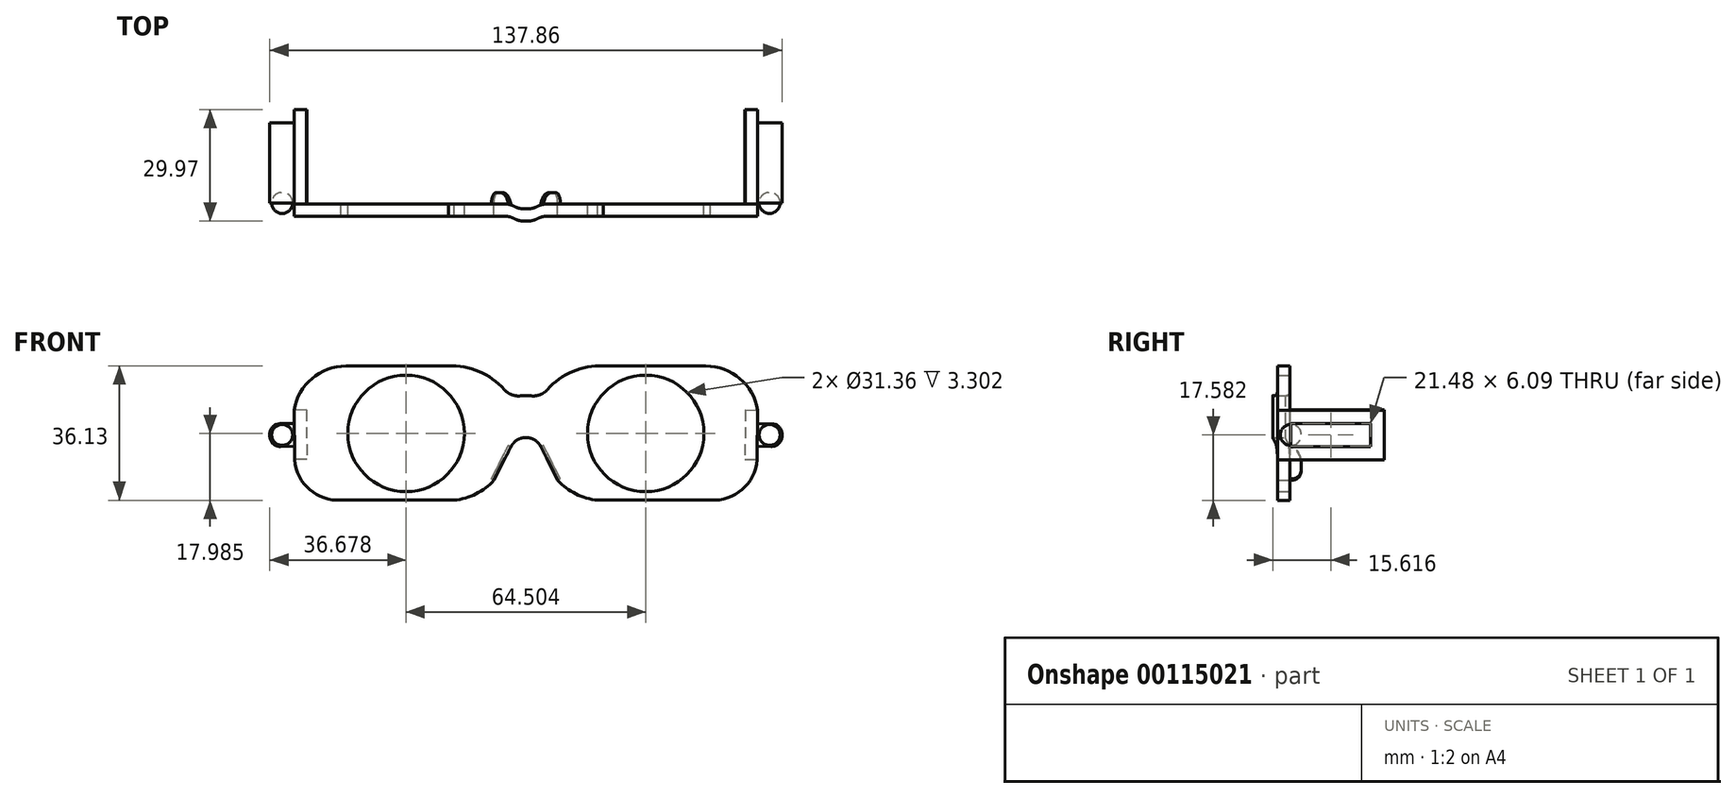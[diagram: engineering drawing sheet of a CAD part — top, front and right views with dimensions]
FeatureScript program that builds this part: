
annotation { "Feature Type Name" : "Feature", "Feature Type Description" : "" }
export const myFeature = defineFeature(function(context is Context, id is Id, definition is map)
    precondition{}
    {
        {
            var Q0;
            Q0=qCreatedBy(makeId("Front.planeOp"),FACE);
            var sketch = newSketch(context, id + "F0", { "sketchPlane" : qUnion([Q0])});
            skArc(sketch, "E0", {"start": v(-62.23, -1.34) * mm, "mid": v(-58.21, -9.35) * mm, "end": v(-49.73, -12.25) * mm});
            skArc(sketch, "E1", {"start": v(-19.33, -12.25) * mm, "mid": v(-13.44, -10.57) * mm, "end": v(-8.57, -6.88) * mm});
            skLineSegment(sketch, "E2", {"start": v(-4, 2.15) * mm, "end": v(-8.57, -6.88) * mm});
            skArc(sketch, "E3.MirrorCS", {"start": v(19.33, -12.25) * mm, "mid": v(13.44, -10.57) * mm, "end": v(8.57, -6.88) * mm});
            skLineSegment(sketch, "E4", {"start": v(4.02, 2.15) * mm, "end": v(8.57, -6.88) * mm});
            skLineSegment(sketch, "E5", {"start": v(-49.73, -12.25) * mm, "end": v(-19.33, -12.25) * mm});
            skArc(sketch, "E6.MirrorCS", {"start": v(62.23, -1.34) * mm, "mid": v(58.21, -9.35) * mm, "end": v(49.73, -12.25) * mm});
            skLineSegment(sketch, "E7", {"start": v(19.33, -12.25) * mm, "end": v(49.73, -12.25) * mm});
            skArc(sketch, "E8", {"start": v(-48.38, 23.83) * mm, "mid": v(-57.58, 20.47) * mm, "end": v(-62.41, 11.96) * mm});
            skLineSegment(sketch, "E9", {"start": v(-62.41, 11.96) * mm, "end": v(-62.23, -1.34) * mm});
            skArc(sketch, "E10.MirrorCS", {"start": v(48.38, 23.83) * mm, "mid": v(57.58, 20.47) * mm, "end": v(62.41, 11.96) * mm});
            skLineSegment(sketch, "E11", {"start": v(62.41, 11.96) * mm, "end": v(62.23, -1.34) * mm});
            skArc(sketch, "E12", {"start": v(4.02, 2.15) * mm, "mid": v(0.01, 4.62) * mm, "end": v(-4, 2.15) * mm});
            skArc(sketch, "E13", {"start": v(-4, 15.1) * mm, "mid": v(-11.25, 21.75) * mm, "end": v(-20.87, 23.83) * mm});
            skArc(sketch, "E14.MirrorCS", {"start": v(4, 15.1) * mm, "mid": v(11.25, 21.75) * mm, "end": v(20.87, 23.83) * mm});
            skLineSegment(sketch, "E15", {"start": v(-48.38, 23.83) * mm, "end": v(-20.87, 23.83) * mm});
            skLineSegment(sketch, "E16", {"start": v(20.87, 23.83) * mm, "end": v(48.38, 23.83) * mm});
            skArc(sketch, "E17", {"start": v(4, 15.1) * mm, "mid": v(0, 15.92) * mm, "end": v(-4, 15.1) * mm});
            skLineSegment(sketch, "E18", {"start": v(-32.25, 21.4) * mm, "end": v(-32.25, -9.96) * mm});
            skLineSegment(sketch, "E19", {"start": v(32.25, 21.4) * mm, "end": v(32.25, -9.96) * mm});
            skArc(sketch, "E20", {"start": v(-32.25, 21.4) * mm, "mid": v(-47.93, 5.71) * mm, "end": v(-32.25, -9.96) * mm});
            skArc(sketch, "E21.MirrorCS", {"start": v(-32.25, 21.4) * mm, "mid": v(-16.57, 5.71) * mm, "end": v(-32.25, -9.96) * mm});
            skArc(sketch, "E22.MirrorCS", {"start": v(32.25, 21.4) * mm, "mid": v(47.93, 5.71) * mm, "end": v(32.25, -9.96) * mm});
            skArc(sketch, "E23.MirrorCS", {"start": v(32.25, 21.4) * mm, "mid": v(16.57, 5.71) * mm, "end": v(32.25, -9.96) * mm});
            skSolve(sketch);
        }
        {
            var Q0;
            Q0=makeQuery(id+"F0.imprint","IMPRINT",FACE,{"disambiguationData":[TD([[makeQuery(id+"F0.imprint","IMPRINT",EDGE,{"derivedFrom":sQuery(id+"F0.wireOp",EDGE,"E0")}),1.0]])]});
            extrude(context, id + "F1", {"entities" : qUnion([Q0]), "depth" : 3.3 * mm});
        }
        {
            var Q0;
            Q0=makeQuery(id+"F1.opExtrude","SWEPT_FACE",FACE,{"disambiguationData":[OSD([sQuery(id+"F0.wireOp",EDGE,"E11")])]});
            var sketch = newSketch(context, id + "F2", { "sketchPlane" : qUnion([Q0])});
            skLineSegment(sketch, "E24", {"start": v(0, 12.8) * mm, "end": v(25.4, 12.8) * mm});
            skLineSegment(sketch, "E25", {"start": v(0, -0.5) * mm, "end": v(25.4, -0.5) * mm});
            skLineSegment(sketch, "E26", {"start": v(25.4, -0.5) * mm, "end": v(25.4, 12.8) * mm});
            skSolve(sketch);
        }
        {
            var Q0;
            Q0=makeQuery(id+"F2.imprint","IMPRINT",FACE,{"disambiguationData":[TD([[makeQuery(id+"F2.imprint","IMPRINT",EDGE,{"derivedFrom":sQuery(id+"F2.wireOp",EDGE,"E24")}),-1.0]])]});
            extrude(context, id + "F3", {"entities" : qUnion([Q0]), "operationType" : NewBodyOperationType.ADD, "oppositeDirection" : true, "depth" : 3.3 * mm});
        }
        {
            var Q0;
            Q0=makeQuery(id+"F1.opExtrude","SWEPT_FACE",FACE,{"disambiguationData":[OSD([sQuery(id+"F0.wireOp",EDGE,"E9")])]});
            var sketch = newSketch(context, id + "F4", { "sketchPlane" : qUnion([Q0])});
            skLineSegment(sketch, "E27", {"start": v(0, 12.8) * mm, "end": v(-25.4, 12.8) * mm});
            skLineSegment(sketch, "E28", {"start": v(-25.4, 12.8) * mm, "end": v(-25.4, -0.5) * mm});
            skLineSegment(sketch, "E29", {"start": v(-25.4, -0.5) * mm, "end": v(0, -0.5) * mm});
            skSolve(sketch);
        }
        {
            var Q0;
            Q0=makeQuery(id+"F4.imprint","IMPRINT",FACE,{"disambiguationData":[TD([[makeQuery(id+"F4.imprint","IMPRINT",EDGE,{"derivedFrom":sQuery(id+"F4.wireOp",EDGE,"E27")}),1.0]])]});
            extrude(context, id + "F5", {"entities" : qUnion([Q0]), "operationType" : NewBodyOperationType.ADD, "oppositeDirection" : true, "depth" : 3.3 * mm});
        }
        {
            var Q0;
            Q0=makeQuery(id+"F1.opExtrude","CAP_FACE",FACE,{"disambiguationData":[OSD([sQuery(id+"F0.wireOp",EDGE,"E0"),sQuery(id+"F0.wireOp",EDGE,"E1"),sQuery(id+"F0.wireOp",EDGE,"E2"),sQuery(id+"F0.wireOp",EDGE,"E3.MirrorCS"),sQuery(id+"F0.wireOp",EDGE,"E4"),sQuery(id+"F0.wireOp",EDGE,"E5"),sQuery(id+"F0.wireOp",EDGE,"E6.MirrorCS"),sQuery(id+"F0.wireOp",EDGE,"E7"),sQuery(id+"F0.wireOp",EDGE,"E8"),sQuery(id+"F0.wireOp",EDGE,"E9"),sQuery(id+"F0.wireOp",EDGE,"E10.MirrorCS"),sQuery(id+"F0.wireOp",EDGE,"E11"),sQuery(id+"F0.wireOp",EDGE,"E12"),sQuery(id+"F0.wireOp",EDGE,"E13"),sQuery(id+"F0.wireOp",EDGE,"E14.MirrorCS"),sQuery(id+"F0.wireOp",EDGE,"E15"),sQuery(id+"F0.wireOp",EDGE,"E16"),sQuery(id+"F0.wireOp",EDGE,"E17"),sQuery(id+"F0.wireOp",EDGE,"F4xOjzNR-pt42-XJaJ-fSFb-Rxwh4oa1ACXs"),sQuery(id+"F0.wireOp",EDGE,"16211c17-e1dd-448f-9ed2-b8a674efdcd80.MirrorC")])],"isStart":true});
            var sketch = newSketch(context, id + "F6", { "sketchPlane" : qUnion([Q0])});
            skLineSegment(sketch, "E30", {"start": v(-8.57, -6.88) * mm, "end": v(-9.25, -6.53) * mm});
            skLineSegment(sketch, "E31", {"start": v(-8.57, -6.88) * mm, "end": v(-4.02, 2.15) * mm});
            skLineSegment(sketch, "E32", {"start": v(-4.02, 2.15) * mm, "end": v(-4.7, 2.5) * mm});
            skLineSegment(sketch, "E33", {"start": v(-9.25, -6.53) * mm, "end": v(-4.7, 2.5) * mm});
            skLineSegment(sketch, "E34.MirrorCS", {"start": v(4.02, 2.15) * mm, "end": v(4.7, 2.5) * mm});
            skLineSegment(sketch, "E35.MirrorCS", {"start": v(8.57, -6.88) * mm, "end": v(9.25, -6.53) * mm});
            skLineSegment(sketch, "E36.MirrorCS", {"start": v(9.25, -6.53) * mm, "end": v(4.7, 2.5) * mm});
            skLineSegment(sketch, "E37.MirrorCS", {"start": v(8.57, -6.88) * mm, "end": v(4.02, 2.15) * mm});
            skSolve(sketch);
        }
        {
            var Q0;
            Q0=makeQuery(id+"F6.imprint","IMPRINT",FACE,{"disambiguationData":[TD([[makeQuery(id+"F6.imprint","IMPRINT",EDGE,{"derivedFrom":sQuery(id+"F6.wireOp",EDGE,"E30")}),-1.0]])]});
            var Q1;
            Q1=makeQuery(id+"F6.imprint","IMPRINT",FACE,{"disambiguationData":[TD([[makeQuery(id+"F6.imprint","IMPRINT",EDGE,{"derivedFrom":sQuery(id+"F6.wireOp",EDGE,"E34.MirrorCS")}),-1.0]])]});
            extrude(context, id + "F7", {"entities" : qUnion([Q0, Q1]), "operationType" : NewBodyOperationType.ADD, "depth" : 3.02 * mm});
        }
        {
            var Q0;
            Q0=makeQuery(id+"F7.opExtrude","CAP_EDGE",EDGE,{"disambiguationData":[OSD([sQuery(id+"F6.wireOp",EDGE,"E30")])],"isStart":false});
            var Q1;
            Q1=makeQuery(id+"F7.opExtrude","CAP_EDGE",EDGE,{"disambiguationData":[OSD([sQuery(id+"F6.wireOp",EDGE,"E35.MirrorCS")])],"isStart":false});
            fillet(context, id + "F8", {"entities" : qUnion([Q0, Q1]), "radius" : 2.54 * mm, "tangentPropagation" : true, "allowEdgeOverflow" : false});
        }
        {
            var Q0;
            Q0=makeQuery(id+"F7.opExtrude","CAP_EDGE",EDGE,{"disambiguationData":[OSD([sQuery(id+"F6.wireOp",EDGE,"E32")])],"isStart":false});
            var Q1;
            Q1=makeQuery(id+"F7.opExtrude","CAP_EDGE",EDGE,{"disambiguationData":[OSD([sQuery(id+"F6.wireOp",EDGE,"E34.MirrorCS")])],"isStart":false});
            fillet(context, id + "F9", {"entities" : qUnion([Q0, Q1]), "radius" : 5.08 * mm, "tangentPropagation" : true, "allowEdgeOverflow" : false});
        }
        {
            var Q0;
            Q0=makeQuery(id+"F1.opExtrude","CAP_FACE",FACE,{"disambiguationData":[OSD([sQuery(id+"F0.wireOp",EDGE,"E0"),sQuery(id+"F0.wireOp",EDGE,"E1"),sQuery(id+"F0.wireOp",EDGE,"E2"),sQuery(id+"F0.wireOp",EDGE,"E3.MirrorCS"),sQuery(id+"F0.wireOp",EDGE,"E4"),sQuery(id+"F0.wireOp",EDGE,"E5"),sQuery(id+"F0.wireOp",EDGE,"E6.MirrorCS"),sQuery(id+"F0.wireOp",EDGE,"E7"),sQuery(id+"F0.wireOp",EDGE,"E8"),sQuery(id+"F0.wireOp",EDGE,"E9"),sQuery(id+"F0.wireOp",EDGE,"E10.MirrorCS"),sQuery(id+"F0.wireOp",EDGE,"E11"),sQuery(id+"F0.wireOp",EDGE,"E12"),sQuery(id+"F0.wireOp",EDGE,"E13"),sQuery(id+"F0.wireOp",EDGE,"E14.MirrorCS"),sQuery(id+"F0.wireOp",EDGE,"E15"),sQuery(id+"F0.wireOp",EDGE,"E16"),sQuery(id+"F0.wireOp",EDGE,"E17"),sQuery(id+"F0.wireOp",EDGE,"F4xOjzNR-pt42-XJaJ-fSFb-Rxwh4oa1ACXs"),sQuery(id+"F0.wireOp",EDGE,"16211c17-e1dd-448f-9ed2-b8a674efdcd80.MirrorC")])],"isStart":false});
            var sketch = newSketch(context, id + "F10", { "sketchPlane" : qUnion([Q0])});
            skLineSegment(sketch, "E38", {"start": v(-4, 15.1) * mm, "end": v(-4, 2.15) * mm});
            skLineSegment(sketch, "E39", {"start": v(4, 15.1) * mm, "end": v(4.02, 2.15) * mm});
            skSolve(sketch);
        }
        {
            var Q0;
            Q0=makeQuery(id+"F10.imprint","IMPRINT",FACE,{"disambiguationData":[TD([[makeQuery(id+"F10.imprint","IMPRINT",EDGE,{"derivedFrom":sQuery(id+"F10.wireOp",EDGE,"E38")}),1.0]])]});
            extrude(context, id + "F11", {"entities" : qUnion([Q0]), "operationType" : NewBodyOperationType.ADD, "depth" : 1.27 * mm});
        }
        {
            var Q0;
            Q0=makeQuery(id+"F11.opExtrude","CAP_EDGE",EDGE,{"disambiguationData":[OSD([sQuery(id+"F10.wireOp",EDGE,"E38")])],"isStart":false});
            var Q1;
            Q1=makeQuery(id+"F11.opExtrude","CAP_EDGE",EDGE,{"disambiguationData":[OSD([sQuery(id+"F10.wireOp",EDGE,"E39")])],"isStart":false});
            fillet(context, id + "F12", {"entities" : qUnion([Q0, Q1]), "radius" : 5.08 * mm, "tangentPropagation" : true, "allowEdgeOverflow" : false});
        }
        {
            var Q0;
            {var subQ0=sQuery(id+"F0.wireOp",EDGE,"E15");var subQ1=sQuery(id+"F0.wireOp",EDGE,"E8");var subQ2=sQuery(id+"F0.wireOp",EDGE,"E13");var subQ3=sQuery(id+"F0.wireOp",EDGE,"E9");var subQ4=sQuery(id+"F0.wireOp",EDGE,"E0");var subQ5=sQuery(id+"F0.wireOp",EDGE,"E17");var subQ6=sQuery(id+"F0.wireOp",EDGE,"F4xOjzNR-pt42-XJaJ-fSFb-Rxwh4oa1ACXs");var subQ7=sQuery(id+"F0.wireOp",EDGE,"E1");var subQ8=sQuery(id+"F0.wireOp",EDGE,"E2");var subQ9=sQuery(id+"F0.wireOp",EDGE,"E12");var subQ10=sQuery(id+"F0.wireOp",EDGE,"E5");var subQ11=sQuery(id+"F10.wireOp",EDGE,"E38");Q0=makeQuery(id+"F12.opFillet","BLEND_EDGE",EDGE,{"blendedFrom":[makeQuery(id+"F11.opExtrude","CAP_EDGE",EDGE,{"disambiguationData":[OSD([subQ11])],"isStart":false}),makeQuery(id+"F11.boolean.opBoolean","SPLIT",FACE,{"disambiguationData":[TD([makeQuery(id+"F1.opExtrude","SWEPT_FACE",FACE,{"disambiguationData":[OSD([subQ4])]})])],"derivedFrom":makeQuery(id+"F1.opExtrude","CAP_FACE",FACE,{"disambiguationData":[OSD([subQ4,subQ7,subQ8,sQuery(id+"F0.wireOp",EDGE,"E3.MirrorCS"),sQuery(id+"F0.wireOp",EDGE,"E4"),subQ10,sQuery(id+"F0.wireOp",EDGE,"E6.MirrorCS"),sQuery(id+"F0.wireOp",EDGE,"E7"),subQ1,subQ3,sQuery(id+"F0.wireOp",EDGE,"E10.MirrorCS"),sQuery(id+"F0.wireOp",EDGE,"E11"),subQ9,subQ2,sQuery(id+"F0.wireOp",EDGE,"E14.MirrorCS"),subQ0,sQuery(id+"F0.wireOp",EDGE,"E16"),subQ5,subQ6,sQuery(id+"F0.wireOp",EDGE,"16211c17-e1dd-448f-9ed2-b8a674efdcd80.MirrorC")])],"isStart":false})})],"blendedInto":[makeQuery(id+"F11.boolean.opBoolean","SPLIT",FACE,{"disambiguationData":[TD([makeQuery(id+"F1.opExtrude","SWEPT_FACE",FACE,{"disambiguationData":[OSD([subQ4])]})])],"derivedFrom":makeQuery(id+"F1.opExtrude","CAP_FACE",FACE,{"disambiguationData":[OSD([subQ4,subQ7,subQ8,sQuery(id+"F0.wireOp",EDGE,"E3.MirrorCS"),sQuery(id+"F0.wireOp",EDGE,"E4"),subQ10,sQuery(id+"F0.wireOp",EDGE,"E6.MirrorCS"),sQuery(id+"F0.wireOp",EDGE,"E7"),subQ1,subQ3,sQuery(id+"F0.wireOp",EDGE,"E10.MirrorCS"),sQuery(id+"F0.wireOp",EDGE,"E11"),subQ9,subQ2,sQuery(id+"F0.wireOp",EDGE,"E14.MirrorCS"),subQ0,sQuery(id+"F0.wireOp",EDGE,"E16"),subQ5,subQ6,sQuery(id+"F0.wireOp",EDGE,"16211c17-e1dd-448f-9ed2-b8a674efdcd80.MirrorC")])],"isStart":false})})]});}
            var Q1;
            {var subQ0=sQuery(id+"F0.wireOp",EDGE,"E17");var subQ1=sQuery(id+"F0.wireOp",EDGE,"E11");var subQ2=sQuery(id+"F0.wireOp",EDGE,"E14.MirrorCS");var subQ3=sQuery(id+"F0.wireOp",EDGE,"E7");var subQ4=sQuery(id+"F0.wireOp",EDGE,"E12");var subQ5=sQuery(id+"F0.wireOp",EDGE,"16211c17-e1dd-448f-9ed2-b8a674efdcd80.MirrorC");var subQ6=sQuery(id+"F0.wireOp",EDGE,"E10.MirrorCS");var subQ7=sQuery(id+"F0.wireOp",EDGE,"E3.MirrorCS");var subQ8=sQuery(id+"F0.wireOp",EDGE,"E16");var subQ9=sQuery(id+"F0.wireOp",EDGE,"E4");var subQ10=sQuery(id+"F0.wireOp",EDGE,"E6.MirrorCS");var subQ11=sQuery(id+"F10.wireOp",EDGE,"E39");Q1=makeQuery(id+"F12.opFillet","BLEND_EDGE",EDGE,{"blendedFrom":[makeQuery(id+"F11.opExtrude","CAP_EDGE",EDGE,{"disambiguationData":[OSD([subQ11])],"isStart":false}),makeQuery(id+"F11.boolean.opBoolean","SPLIT",FACE,{"disambiguationData":[TD([makeQuery(id+"F1.opExtrude","SWEPT_FACE",FACE,{"disambiguationData":[OSD([subQ7])]})])],"derivedFrom":makeQuery(id+"F1.opExtrude","CAP_FACE",FACE,{"disambiguationData":[OSD([sQuery(id+"F0.wireOp",EDGE,"E0"),sQuery(id+"F0.wireOp",EDGE,"E1"),sQuery(id+"F0.wireOp",EDGE,"E2"),subQ7,subQ9,sQuery(id+"F0.wireOp",EDGE,"E5"),subQ10,subQ3,sQuery(id+"F0.wireOp",EDGE,"E8"),sQuery(id+"F0.wireOp",EDGE,"E9"),subQ6,subQ1,subQ4,sQuery(id+"F0.wireOp",EDGE,"E13"),subQ2,sQuery(id+"F0.wireOp",EDGE,"E15"),subQ8,subQ0,sQuery(id+"F0.wireOp",EDGE,"F4xOjzNR-pt42-XJaJ-fSFb-Rxwh4oa1ACXs"),subQ5])],"isStart":false})})],"blendedInto":[makeQuery(id+"F11.boolean.opBoolean","SPLIT",FACE,{"disambiguationData":[TD([makeQuery(id+"F1.opExtrude","SWEPT_FACE",FACE,{"disambiguationData":[OSD([subQ7])]})])],"derivedFrom":makeQuery(id+"F1.opExtrude","CAP_FACE",FACE,{"disambiguationData":[OSD([sQuery(id+"F0.wireOp",EDGE,"E0"),sQuery(id+"F0.wireOp",EDGE,"E1"),sQuery(id+"F0.wireOp",EDGE,"E2"),subQ7,subQ9,sQuery(id+"F0.wireOp",EDGE,"E5"),subQ10,subQ3,sQuery(id+"F0.wireOp",EDGE,"E8"),sQuery(id+"F0.wireOp",EDGE,"E9"),subQ6,subQ1,subQ4,sQuery(id+"F0.wireOp",EDGE,"E13"),subQ2,sQuery(id+"F0.wireOp",EDGE,"E15"),subQ8,subQ0,sQuery(id+"F0.wireOp",EDGE,"F4xOjzNR-pt42-XJaJ-fSFb-Rxwh4oa1ACXs"),subQ5])],"isStart":false})})]});}
            fillet(context, id + "F13", {"entities" : qUnion([Q0, Q1]), "radius" : 5.08 * mm, "tangentPropagation" : true, "allowEdgeOverflow" : false});
        }
        {
            var Q0;
            Q0=makeQuery(id+"F1.opExtrude","SWEPT_EDGE",EDGE,{"disambiguationData":[OSD([sQuery(id+"F0.wireOp",EDGE,"E13"),sQuery(id+"F0.wireOp",EDGE,"E17")])]});
            var Q1;
            Q1=makeQuery(id+"F1.opExtrude","SWEPT_EDGE",EDGE,{"disambiguationData":[OSD([sQuery(id+"F0.wireOp",EDGE,"E14.MirrorCS"),sQuery(id+"F0.wireOp",EDGE,"E17")])]});
            fillet(context, id + "F14", {"entities" : qUnion([Q0, Q1]), "radius" : 5.08 * mm, "tangentPropagation" : true, "allowEdgeOverflow" : false});
        }
        {
            var Q0;
            Q0=makeQuery(id+"F1.opExtrude","CAP_FACE",FACE,{"disambiguationData":[OSD([sQuery(id+"F0.wireOp",EDGE,"E0"),sQuery(id+"F0.wireOp",EDGE,"E1"),sQuery(id+"F0.wireOp",EDGE,"E2"),sQuery(id+"F0.wireOp",EDGE,"E3.MirrorCS"),sQuery(id+"F0.wireOp",EDGE,"E4"),sQuery(id+"F0.wireOp",EDGE,"E5"),sQuery(id+"F0.wireOp",EDGE,"E6.MirrorCS"),sQuery(id+"F0.wireOp",EDGE,"E7"),sQuery(id+"F0.wireOp",EDGE,"E8"),sQuery(id+"F0.wireOp",EDGE,"E9"),sQuery(id+"F0.wireOp",EDGE,"E10.MirrorCS"),sQuery(id+"F0.wireOp",EDGE,"E11"),sQuery(id+"F0.wireOp",EDGE,"E12"),sQuery(id+"F0.wireOp",EDGE,"E13"),sQuery(id+"F0.wireOp",EDGE,"E14.MirrorCS"),sQuery(id+"F0.wireOp",EDGE,"E15"),sQuery(id+"F0.wireOp",EDGE,"E16"),sQuery(id+"F0.wireOp",EDGE,"E17"),sQuery(id+"F0.wireOp",EDGE,"F4xOjzNR-pt42-XJaJ-fSFb-Rxwh4oa1ACXs"),sQuery(id+"F0.wireOp",EDGE,"16211c17-e1dd-448f-9ed2-b8a674efdcd80.MirrorC")])],"isStart":true});
            var sketch = newSketch(context, id + "F15", { "sketchPlane" : qUnion([Q0])});
            skLineSegment(sketch, "E40", {"start": v(-4.02, 2.15) * mm, "end": v(-4.02, 16.21) * mm});
            skLineSegment(sketch, "E41.MirrorCS", {"start": v(4, 2.15) * mm, "end": v(4, 16.21) * mm});
            skSolve(sketch);
        }
        {
            var Q0;
            {var subQ11=sQuery(id+"F15.wireOp",EDGE,"E40");Q0=makeQuery(id+"F15.imprint","IMPRINT",FACE,{"disambiguationData":[TD([[makeQuery(id+"F15.imprint","IMPRINT",EDGE,{"derivedFrom":subQ11}),-1.0]])]});}
            extrude(context, id + "F16", {"entities" : qUnion([Q0]), "operationType" : NewBodyOperationType.REMOVE, "oppositeDirection" : true, "depth" : 1.27 * mm});
        }
        {
            var Q0;
            Q0=makeQuery(id+"F16.boolean.opBoolean","COPY",EDGE,{"derivedFrom":makeQuery(id+"F16.opExtrude","CAP_EDGE",EDGE,{"disambiguationData":[OSD([sQuery(id+"F15.wireOp",EDGE,"E40")])],"isStart":false})});
            var Q1;
            Q1=makeQuery(id+"F16.boolean.opBoolean","COPY",EDGE,{"derivedFrom":makeQuery(id+"F16.opExtrude","CAP_EDGE",EDGE,{"disambiguationData":[OSD([sQuery(id+"F15.wireOp",EDGE,"E41.MirrorCS")])],"isStart":false})});
            fillet(context, id + "F17", {"entities" : qUnion([Q0, Q1]), "radius" : 5.08 * mm, "tangentPropagation" : true, "allowEdgeOverflow" : false});
        }
        {
            var Q0;
            {var subQ0=sQuery(id+"F0.wireOp",EDGE,"E14.MirrorCS");var subQ1=sQuery(id+"F0.wireOp",EDGE,"E7");var subQ2=sQuery(id+"F0.wireOp",EDGE,"E17");var subQ3=sQuery(id+"F0.wireOp",EDGE,"16211c17-e1dd-448f-9ed2-b8a674efdcd80.MirrorC");var subQ4=sQuery(id+"F15.wireOp",EDGE,"E40");var subQ5=sQuery(id+"F0.wireOp",EDGE,"E11");var subQ7=sQuery(id+"F0.wireOp",EDGE,"E10.MirrorCS");var subQ8=sQuery(id+"F0.wireOp",EDGE,"E3.MirrorCS");var subQ9=sQuery(id+"F0.wireOp",EDGE,"E16");var subQ10=sQuery(id+"F0.wireOp",EDGE,"E4");var subQ11=sQuery(id+"F0.wireOp",EDGE,"E6.MirrorCS");Q0=makeQuery(id+"F17.opFillet","BLEND_EDGE",EDGE,{"blendedFrom":[makeQuery(id+"F16.boolean.opBoolean","COPY",EDGE,{"derivedFrom":makeQuery(id+"F16.opExtrude","CAP_EDGE",EDGE,{"disambiguationData":[OSD([subQ4])],"isStart":false})}),makeQuery(id+"F16.boolean.opBoolean","SPLIT",FACE,{"disambiguationData":[TD([makeQuery(id+"F1.opExtrude","SWEPT_FACE",FACE,{"disambiguationData":[OSD([subQ8])]})])],"derivedFrom":makeQuery(id+"F1.opExtrude","CAP_FACE",FACE,{"disambiguationData":[OSD([sQuery(id+"F0.wireOp",EDGE,"E0"),sQuery(id+"F0.wireOp",EDGE,"E1"),sQuery(id+"F0.wireOp",EDGE,"E2"),subQ8,subQ10,sQuery(id+"F0.wireOp",EDGE,"E5"),subQ11,subQ1,sQuery(id+"F0.wireOp",EDGE,"E8"),sQuery(id+"F0.wireOp",EDGE,"E9"),subQ7,subQ5,sQuery(id+"F0.wireOp",EDGE,"E12"),sQuery(id+"F0.wireOp",EDGE,"E13"),subQ0,sQuery(id+"F0.wireOp",EDGE,"E15"),subQ9,subQ2,sQuery(id+"F0.wireOp",EDGE,"F4xOjzNR-pt42-XJaJ-fSFb-Rxwh4oa1ACXs"),subQ3])],"isStart":true})})],"blendedInto":[makeQuery(id+"F16.boolean.opBoolean","SPLIT",FACE,{"disambiguationData":[TD([makeQuery(id+"F1.opExtrude","SWEPT_FACE",FACE,{"disambiguationData":[OSD([subQ8])]})])],"derivedFrom":makeQuery(id+"F1.opExtrude","CAP_FACE",FACE,{"disambiguationData":[OSD([sQuery(id+"F0.wireOp",EDGE,"E0"),sQuery(id+"F0.wireOp",EDGE,"E1"),sQuery(id+"F0.wireOp",EDGE,"E2"),subQ8,subQ10,sQuery(id+"F0.wireOp",EDGE,"E5"),subQ11,subQ1,sQuery(id+"F0.wireOp",EDGE,"E8"),sQuery(id+"F0.wireOp",EDGE,"E9"),subQ7,subQ5,sQuery(id+"F0.wireOp",EDGE,"E12"),sQuery(id+"F0.wireOp",EDGE,"E13"),subQ0,sQuery(id+"F0.wireOp",EDGE,"E15"),subQ9,subQ2,sQuery(id+"F0.wireOp",EDGE,"F4xOjzNR-pt42-XJaJ-fSFb-Rxwh4oa1ACXs"),subQ3])],"isStart":true})})]});}
            var Q1;
            {var subQ1=sQuery(id+"F15.wireOp",EDGE,"E41.MirrorCS");var subQ2=sQuery(id+"F0.wireOp",EDGE,"F4xOjzNR-pt42-XJaJ-fSFb-Rxwh4oa1ACXs");var subQ3=sQuery(id+"F0.wireOp",EDGE,"E15");var subQ4=sQuery(id+"F0.wireOp",EDGE,"E8");var subQ5=sQuery(id+"F0.wireOp",EDGE,"E13");var subQ8=sQuery(id+"F0.wireOp",EDGE,"E9");var subQ9=sQuery(id+"F0.wireOp",EDGE,"E0");var subQ10=sQuery(id+"F0.wireOp",EDGE,"E1");var subQ11=sQuery(id+"F0.wireOp",EDGE,"E2");var subQ12=sQuery(id+"F0.wireOp",EDGE,"E5");var subQ13=sQuery(id+"F0.wireOp",EDGE,"E17");Q1=makeQuery(id+"F17.opFillet","BLEND_EDGE",EDGE,{"blendedFrom":[makeQuery(id+"F16.boolean.opBoolean","COPY",EDGE,{"derivedFrom":makeQuery(id+"F16.opExtrude","CAP_EDGE",EDGE,{"disambiguationData":[OSD([subQ1])],"isStart":false})}),makeQuery(id+"F16.boolean.opBoolean","SPLIT",FACE,{"disambiguationData":[TD([makeQuery(id+"F1.opExtrude","SWEPT_FACE",FACE,{"disambiguationData":[OSD([subQ9])]})])],"derivedFrom":makeQuery(id+"F1.opExtrude","CAP_FACE",FACE,{"disambiguationData":[OSD([subQ9,subQ10,subQ11,sQuery(id+"F0.wireOp",EDGE,"E3.MirrorCS"),sQuery(id+"F0.wireOp",EDGE,"E4"),subQ12,sQuery(id+"F0.wireOp",EDGE,"E6.MirrorCS"),sQuery(id+"F0.wireOp",EDGE,"E7"),subQ4,subQ8,sQuery(id+"F0.wireOp",EDGE,"E10.MirrorCS"),sQuery(id+"F0.wireOp",EDGE,"E11"),sQuery(id+"F0.wireOp",EDGE,"E12"),subQ5,sQuery(id+"F0.wireOp",EDGE,"E14.MirrorCS"),subQ3,sQuery(id+"F0.wireOp",EDGE,"E16"),subQ13,subQ2,sQuery(id+"F0.wireOp",EDGE,"16211c17-e1dd-448f-9ed2-b8a674efdcd80.MirrorC")])],"isStart":true})})],"blendedInto":[makeQuery(id+"F16.boolean.opBoolean","SPLIT",FACE,{"disambiguationData":[TD([makeQuery(id+"F1.opExtrude","SWEPT_FACE",FACE,{"disambiguationData":[OSD([subQ9])]})])],"derivedFrom":makeQuery(id+"F1.opExtrude","CAP_FACE",FACE,{"disambiguationData":[OSD([subQ9,subQ10,subQ11,sQuery(id+"F0.wireOp",EDGE,"E3.MirrorCS"),sQuery(id+"F0.wireOp",EDGE,"E4"),subQ12,sQuery(id+"F0.wireOp",EDGE,"E6.MirrorCS"),sQuery(id+"F0.wireOp",EDGE,"E7"),subQ4,subQ8,sQuery(id+"F0.wireOp",EDGE,"E10.MirrorCS"),sQuery(id+"F0.wireOp",EDGE,"E11"),sQuery(id+"F0.wireOp",EDGE,"E12"),subQ5,sQuery(id+"F0.wireOp",EDGE,"E14.MirrorCS"),subQ3,sQuery(id+"F0.wireOp",EDGE,"E16"),subQ13,subQ2,sQuery(id+"F0.wireOp",EDGE,"16211c17-e1dd-448f-9ed2-b8a674efdcd80.MirrorC")])],"isStart":true})})]});}
            fillet(context, id + "F18", {"entities" : qUnion([Q0, Q1]), "radius" : 5.08 * mm, "tangentPropagation" : true, "allowEdgeOverflow" : false});
        }
        {
            var Q0;
            {var subQ0=sQuery(id+"F0.wireOp",EDGE,"E9");Q0=makeQuery(id+"F5.boolean.opBoolean","MERGE",FACE,{"derivedFrom":[makeQuery(id+"F1.opExtrude","SWEPT_FACE",FACE,{"disambiguationData":[OSD([subQ0])]}),makeQuery(id+"F5.opExtrude","CAP_FACE",FACE,{"disambiguationData":[OSD([subQ0,sQuery(id+"F4.wireOp",EDGE,"E27"),sQuery(id+"F4.wireOp",EDGE,"E28"),sQuery(id+"F4.wireOp",EDGE,"E29")])],"isStart":true})]});}
            var sketch = newSketch(context, id + "F19", { "sketchPlane" : qUnion([Q0])});
            skLineSegment(sketch, "E42.0", {"start": v(-0.3, 9.21) * mm, "end": v(-21.8, 9.21) * mm});
            skLineSegment(sketch, "E42.1", {"start": v(-0.3, 9.21) * mm, "end": v(-0.3, 3.1) * mm});
            skLineSegment(sketch, "E42.2", {"start": v(-21.8, 3.1) * mm, "end": v(-0.3, 3.1) * mm});
            skLineSegment(sketch, "E42.3", {"start": v(-21.8, 9.21) * mm, "end": v(-21.8, 3.1) * mm});
            skSolve(sketch);
        }
        {
            var Q0;
            {var subQ0=sQuery(id+"F0.wireOp",EDGE,"E11");Q0=makeQuery(id+"F3.boolean.opBoolean","MERGE",FACE,{"derivedFrom":[makeQuery(id+"F1.opExtrude","SWEPT_FACE",FACE,{"disambiguationData":[OSD([subQ0])]}),makeQuery(id+"F3.opExtrude","CAP_FACE",FACE,{"disambiguationData":[OSD([subQ0,sQuery(id+"F2.wireOp",EDGE,"E24"),sQuery(id+"F2.wireOp",EDGE,"E25"),sQuery(id+"F2.wireOp",EDGE,"E26")])],"isStart":true})]});}
            var sketch = newSketch(context, id + "F20", { "sketchPlane" : qUnion([Q0])});
            skLineSegment(sketch, "E43.0", {"start": v(0.3, 9.2) * mm, "end": v(21.79, 9.2) * mm});
            skLineSegment(sketch, "E43.1", {"start": v(0.3, 9.2) * mm, "end": v(0.3, 3.1) * mm});
            skLineSegment(sketch, "E43.2", {"start": v(0.3, 3.1) * mm, "end": v(21.79, 3.1) * mm});
            skLineSegment(sketch, "E43.3", {"start": v(21.79, 3.1) * mm, "end": v(21.79, 9.2) * mm});
            skSolve(sketch);
        }
        {
            var Q0;
            Q0=makeQuery(id+"F20.imprint","IMPRINT",FACE,{"disambiguationData":[TD([[makeQuery(id+"F20.imprint","IMPRINT",EDGE,{"derivedFrom":sQuery(id+"F20.wireOp",EDGE,"E43.0")}),-1.0]])]});
            extrude(context, id + "F21", {"entities" : qUnion([Q0]), "operationType" : NewBodyOperationType.ADD, "depth" : 6.6 * mm});
        }
        {
            var Q0;
            Q0=makeQuery(id+"F19.imprint","IMPRINT",FACE,{"disambiguationData":[TD([[makeQuery(id+"F19.imprint","IMPRINT",EDGE,{"derivedFrom":sQuery(id+"F19.wireOp",EDGE,"E42.0")}),1.0]])]});
            extrude(context, id + "F22", {"entities" : qUnion([Q0]), "operationType" : NewBodyOperationType.ADD, "depth" : 6.6 * mm});
        }
        {
            var Q0;
            Q0=makeQuery(id+"F22.opExtrude","CAP_EDGE",EDGE,{"disambiguationData":[OSD([sQuery(id+"F19.wireOp",EDGE,"E42.0")])],"isStart":false});
            var Q1;
            Q1=makeQuery(id+"F22.opExtrude","CAP_EDGE",EDGE,{"disambiguationData":[OSD([sQuery(id+"F19.wireOp",EDGE,"E42.2")])],"isStart":false});
            var Q2;
            Q2=makeQuery(id+"F21.opExtrude","CAP_EDGE",EDGE,{"disambiguationData":[OSD([sQuery(id+"F20.wireOp",EDGE,"E43.2")])],"isStart":false});
            var Q3;
            Q3=makeQuery(id+"F21.opExtrude","CAP_EDGE",EDGE,{"disambiguationData":[OSD([sQuery(id+"F20.wireOp",EDGE,"E43.0")])],"isStart":false});
            fillet(context, id + "F23", {"entities" : qUnion([Q0, Q1, Q2, Q3]), "radius" : 2.8 * mm, "tangentPropagation" : true, "allowEdgeOverflow" : false});
        }
        {
            var Q0;
            Q0=makeQuery(id+"F22.opExtrude","SWEPT_FACE",FACE,{"disambiguationData":[OSD([sQuery(id+"F19.wireOp",EDGE,"E42.1")])]});
            var sketch = newSketch(context, id + "F24", { "sketchPlane" : qUnion([Q0])});
            skCircle(sketch, "E44", {"center": v(-65.58, 5.31) * mm, "radius": 2.83 * mm});
            skPoint(sketch, "E44.centerSnap0", {"position": v(-62.32, 5.31) * mm});
            skCircle(sketch, "E45.MirrorC", {"center": v(65.58, 5.31) * mm, "radius": 2.83 * mm});
            skLineSegment(sketch, "E46", {"start": v(-65.58, 8.14) * mm, "end": v(-65.58, 2.48) * mm});
            skLineSegment(sketch, "E47", {"start": v(65.58, 8.14) * mm, "end": v(65.58, 2.48) * mm});
            skSolve(sketch);
        }
        {
            var Q0;
            {var subQ0=sQuery(id+"F24.wireOp",EDGE,"E46");Q0=makeQuery(id+"F24.imprint","IMPRINT",FACE,{"disambiguationData":[TD([[makeQuery(id+"F24.imprint","IMPRINT",EDGE,{"derivedFrom":subQ0}),-1.0]])]});}
            var Q1;
            Q1=sQuery(id+"F24.wireOp",EDGE,"E46");
            revolve(context, id + "F25", {"entities" : qUnion([Q0]), "axis" : qUnion([Q1]), "revolveType" : RevolveType.FULL});
        }
        {
            var Q0;
            {var subQ0=sQuery(id+"F24.wireOp",EDGE,"E47");Q0=makeQuery(id+"F24.imprint","IMPRINT",FACE,{"disambiguationData":[TD([[makeQuery(id+"F24.imprint","IMPRINT",EDGE,{"derivedFrom":subQ0}),-1.0]])]});}
            var Q1;
            Q1=sQuery(id+"F24.wireOp",EDGE,"E47");
            revolve(context, id + "F26", {"entities" : qUnion([Q0]), "axis" : qUnion([Q1]), "revolveType" : RevolveType.FULL});
        }
        {
            var Q0;
            Q0=sQuery(id+"F0.wireOp",EDGE,"E20");
            var Q1;
            Q1=sQuery(id+"F0.wireOp",EDGE,"E18");
            revolve(context, id + "F27", {"bodyType" : ToolBodyType.SURFACE, "surfaceEntities" : qUnion([Q0]), "axis" : qUnion([Q1]), "revolveType" : RevolveType.ONE_DIRECTION, "oppositeDirection" : true, "angle" : 180 * degree});
        }
        {
            var Q0;
            Q0=sQuery(id+"F0.wireOp",EDGE,"E23.MirrorCS");
            var Q1;
            Q1=sQuery(id+"F0.wireOp",EDGE,"E19");
            revolve(context, id + "F28", {"bodyType" : ToolBodyType.SURFACE, "surfaceEntities" : qUnion([Q0]), "axis" : qUnion([Q1]), "revolveType" : RevolveType.ONE_DIRECTION, "oppositeDirection" : true, "angle" : 180 * degree});
        }
    });
